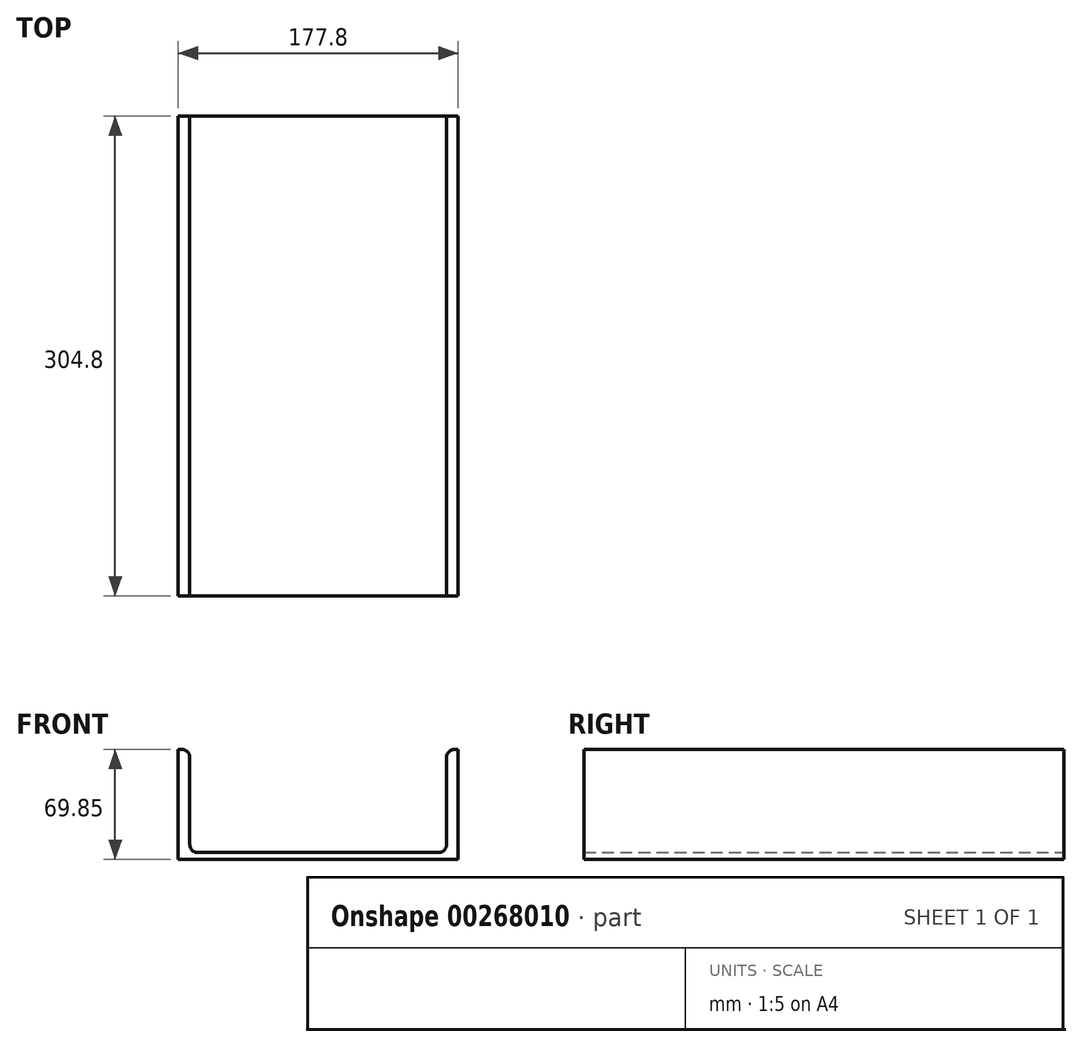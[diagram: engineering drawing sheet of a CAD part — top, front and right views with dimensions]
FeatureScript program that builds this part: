
annotation { "Feature Type Name" : "Feature", "Feature Type Description" : "" }
export const myFeature = defineFeature(function(context is Context, id is Id, definition is map)
    precondition{}
    {
        {
            var Q0;
            Q0=qCreatedBy(makeId("Front.planeOp"),FACE);
            var sketch = newSketch(context, id + "F0", { "sketchPlane" : qUnion([Q0])});
            skLineSegment(sketch, "E0.bottom", {"start": v(0, 0) * mm, "end": v(177.8, 0) * mm});
            skLineSegment(sketch, "E0.top", {"start": v(0, 69.85) * mm, "end": v(7.37, 69.85) * mm});
            skLineSegment(sketch, "E0.left", {"start": v(0, 0) * mm, "end": v(0, 69.85) * mm});
            skLineSegment(sketch, "E0.right", {"start": v(177.8, 0) * mm, "end": v(177.8, 69.85) * mm});
            skLineSegment(sketch, "E1.top", {"start": v(7.37, 4.32) * mm, "end": v(170.43, 4.32) * mm});
            skLineSegment(sketch, "E1.left", {"start": v(7.37, 69.85) * mm, "end": v(7.37, 4.32) * mm});
            skLineSegment(sketch, "E1.right", {"start": v(170.43, 69.85) * mm, "end": v(170.43, 4.32) * mm});
            skLineSegment(sketch, "E2.trimOffspring", {"start": v(170.43, 69.85) * mm, "end": v(177.8, 69.85) * mm});
            skSolve(sketch);
        }
        {
            var Q0;
            Q0 = qSketchRegion(id + "F0", true);
            extrude(context, id + "F1", {"entities" : qUnion([Q0]), "depth" : 304.8 * mm});
        }
        {
            var Q0;
            Q0=makeQuery(id+"F1.opExtrude","SWEPT_EDGE",EDGE,{"disambiguationData":[OSD([sQuery(id+"F0.wireOp",EDGE,"E0.top"),sQuery(id+"F0.wireOp",EDGE,"E1.left")])]});
            var Q1;
            Q1=makeQuery(id+"F1.opExtrude","SWEPT_EDGE",EDGE,{"disambiguationData":[OSD([sQuery(id+"F0.wireOp",EDGE,"E1.right"),sQuery(id+"F0.wireOp",EDGE,"E2.trimOffspring")])]});
            var Q2;
            Q2=makeQuery(id+"F1.opExtrude","SWEPT_EDGE",EDGE,{"disambiguationData":[OSD([sQuery(id+"F0.wireOp",EDGE,"E1.top"),sQuery(id+"F0.wireOp",EDGE,"E1.left")])]});
            var Q3;
            Q3=makeQuery(id+"F1.opExtrude","SWEPT_EDGE",EDGE,{"disambiguationData":[OSD([sQuery(id+"F0.wireOp",EDGE,"E1.top"),sQuery(id+"F0.wireOp",EDGE,"E1.right")])]});
            fillet(context, id + "F2", {"entities" : qUnion([Q0, Q1, Q2, Q3]), "radius" : 5.08 * mm, "tangentPropagation" : true, "allowEdgeOverflow" : false});
        }
    });
